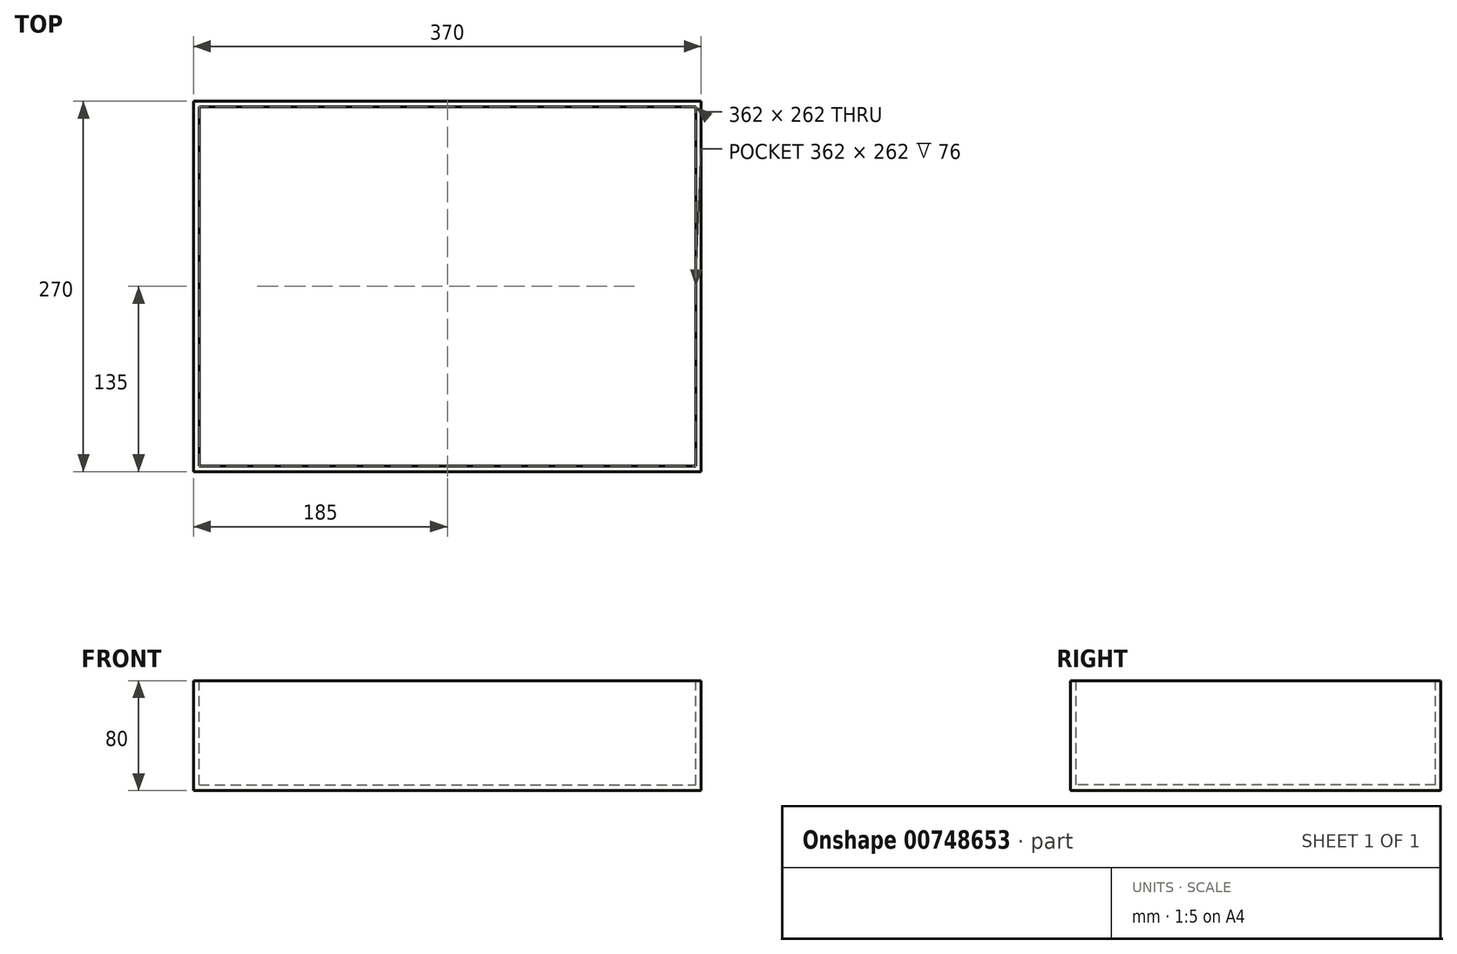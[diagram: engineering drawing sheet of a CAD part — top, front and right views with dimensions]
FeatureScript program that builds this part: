
annotation { "Feature Type Name" : "Feature", "Feature Type Description" : "" }
export const myFeature = defineFeature(function(context is Context, id is Id, definition is map)
    precondition{}
    {
        {
            var Q0;
            Q0=qCreatedBy(makeId("Top.planeOp"),FACE);
            var sketch = newSketch(context, id + "F0", { "sketchPlane" : qUnion([Q0])});
            skLineSegment(sketch, "E0.bottom", {"start": v(-370, 270) * mm, "end": v(0, 270) * mm});
            skLineSegment(sketch, "E0.top", {"start": v(-370, 0) * mm, "end": v(0, 0) * mm});
            skLineSegment(sketch, "E0.left", {"start": v(-370, 270) * mm, "end": v(-370, 0) * mm});
            skLineSegment(sketch, "E0.right", {"start": v(0, 270) * mm, "end": v(0, 0) * mm});
            skSolve(sketch);
        }
        {
            var Q0;
            Q0=makeQuery(id+"F0.imprint","IMPRINT",FACE,{"disambiguationData":[TD([[makeQuery(id+"F0.imprint","IMPRINT",EDGE,{"derivedFrom":sQuery(id+"F0.wireOp",EDGE,"E0.bottom")}),-1.0]])]});
            extrude(context, id + "F1", {"entities" : qUnion([Q0]), "oppositeDirection" : true, "depth" : 80 * mm, "offsetDistance" : 25 * mm});
        }
        {
            var Q0;
            Q0=makeQuery(id+"F1.opExtrude","CAP_FACE",FACE,{"disambiguationData":[OSD([sQuery(id+"F0.wireOp",EDGE,"E0.bottom"),sQuery(id+"F0.wireOp",EDGE,"E0.top"),sQuery(id+"F0.wireOp",EDGE,"E0.left"),sQuery(id+"F0.wireOp",EDGE,"E0.right")])],"isStart":true});
            var sketch = newSketch(context, id + "F2", { "sketchPlane" : qUnion([Q0])});
            skLineSegment(sketch, "E1.bottom", {"start": v(-366, 266) * mm, "end": v(-4, 266) * mm});
            skLineSegment(sketch, "E1.top", {"start": v(-366, 4) * mm, "end": v(-4, 4) * mm});
            skLineSegment(sketch, "E1.left", {"start": v(-366, 266) * mm, "end": v(-366, 4) * mm});
            skLineSegment(sketch, "E1.right", {"start": v(-4, 266) * mm, "end": v(-4, 4) * mm});
            skSolve(sketch);
        }
        {
            var Q0;
            Q0=makeQuery(id+"F2.imprint","IMPRINT",FACE,{"disambiguationData":[TD([[makeQuery(id+"F2.imprint","IMPRINT",EDGE,{"derivedFrom":sQuery(id+"F2.wireOp",EDGE,"E1.bottom")}),-1.0]])]});
            extrude(context, id + "F3", {"entities" : qUnion([Q0]), "operationType" : NewBodyOperationType.REMOVE, "oppositeDirection" : true, "depth" : 76 * mm, "offsetDistance" : 25 * mm});
        }
    });
